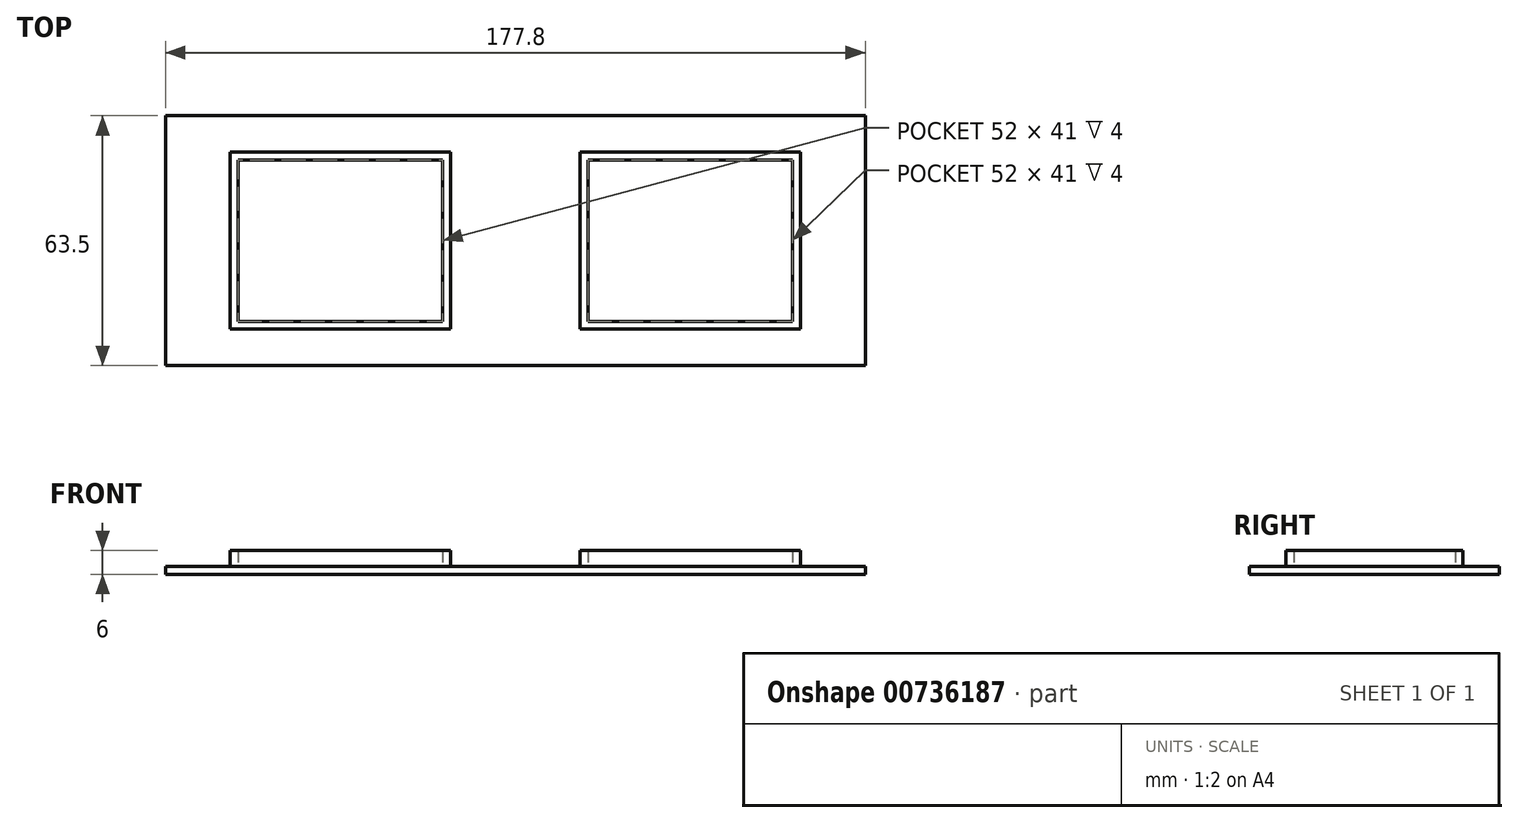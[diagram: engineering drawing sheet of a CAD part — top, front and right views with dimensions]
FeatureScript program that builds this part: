
annotation { "Feature Type Name" : "Feature", "Feature Type Description" : "" }
export const myFeature = defineFeature(function(context is Context, id is Id, definition is map)
    precondition{}
    {
        {
            var Q0;
            Q0=qCreatedBy(makeId("Top.planeOp"),FACE);
            var sketch = newSketch(context, id + "F0", { "sketchPlane" : qUnion([Q0])});
            skLineSegment(sketch, "E0.bottom", {"start": v(0, 0) * mm, "end": v(88.9, 0) * mm});
            skLineSegment(sketch, "E0.top", {"start": v(0, 63.5) * mm, "end": v(88.9, 63.5) * mm});
            skLineSegment(sketch, "E0.left", {"start": v(0, 0) * mm, "end": v(0, 63.5) * mm});
            skLineSegment(sketch, "E0.right", {"start": v(88.9, 0) * mm, "end": v(88.9, 63.5) * mm});
            skLineSegment(sketch, "E1", {"start": v(44.45, 0) * mm, "end": v(44.45, 63.5) * mm, "construction": true});
            skLineSegment(sketch, "E2", {"start": v(0, 31.75) * mm, "end": v(88.9, 31.75) * mm, "construction": true});
            skLineSegment(sketch, "E3.bottom", {"start": v(70.45, 52.25) * mm, "end": v(18.45, 52.25) * mm});
            skLineSegment(sketch, "E3.top", {"start": v(70.45, 11.25) * mm, "end": v(18.45, 11.25) * mm});
            skLineSegment(sketch, "E3.left", {"start": v(70.45, 52.25) * mm, "end": v(70.45, 11.25) * mm});
            skLineSegment(sketch, "E3.right", {"start": v(18.45, 52.25) * mm, "end": v(18.45, 11.25) * mm});
            skPoint(sketch, "E3.middle", {"position": v(44.45, 31.75) * mm});
            skLineSegment(sketch, "E4.bottom", {"start": v(16.45, 54.25) * mm, "end": v(72.45, 54.25) * mm});
            skLineSegment(sketch, "E4.top", {"start": v(16.45, 9.25) * mm, "end": v(72.45, 9.25) * mm});
            skLineSegment(sketch, "E4.left", {"start": v(16.45, 54.25) * mm, "end": v(16.45, 9.25) * mm});
            skLineSegment(sketch, "E4.right", {"start": v(72.45, 54.25) * mm, "end": v(72.45, 9.25) * mm});
            skSolve(sketch);
        }
        {
            var Q0;
            Q0=makeQuery(id+"F0.imprint","IMPRINT",FACE,{"disambiguationData":[TD([[makeQuery(id+"F0.imprint","IMPRINT",EDGE,{"derivedFrom":sQuery(id+"F0.wireOp",EDGE,"E3.bottom")}),-1.0]])]});
            extrude(context, id + "F1", {"entities" : qUnion([Q0]), "depth" : 6 * mm, "offsetDistance" : 25 * mm});
        }
        {
            var Q0;
            Q0=makeQuery(id+"F0.imprint","IMPRINT",FACE,{"disambiguationData":[TD([[makeQuery(id+"F0.imprint","IMPRINT",EDGE,{"derivedFrom":sQuery(id+"F0.wireOp",EDGE,"E0.bottom")}),1.0]])]});
            extrude(context, id + "F2", {"entities" : qUnion([Q0]), "operationType" : NewBodyOperationType.ADD, "depth" : 2 * mm, "offsetDistance" : 25 * mm});
        }
        {
            var Q0;
            Q0=makeQuery(id+"F0.imprint","IMPRINT",FACE,{"disambiguationData":[TD([[makeQuery(id+"F0.imprint","IMPRINT",EDGE,{"derivedFrom":sQuery(id+"F0.wireOp",EDGE,"E3.bottom")}),1.0]])]});
            extrude(context, id + "F3", {"entities" : qUnion([Q0]), "depth" : 2 * mm, "offsetDistance" : 25 * mm});
        }
        {
            var Q0;
            Q0=makeQuery(id+"F3.opExtrude","SWEPT_BODY",BODY,{"disambiguationData":[OSD([sQuery(id+"F0.wireOp",EDGE,"E3.bottom"),sQuery(id+"F0.wireOp",EDGE,"E3.top"),sQuery(id+"F0.wireOp",EDGE,"E3.left"),sQuery(id+"F0.wireOp",EDGE,"E3.right")])]});
            var Q1;
            Q1=makeQuery(id+"F1.opExtrude","SWEPT_BODY",BODY,{"disambiguationData":[OSD([sQuery(id+"F0.wireOp",EDGE,"E3.bottom"),sQuery(id+"F0.wireOp",EDGE,"E3.top"),sQuery(id+"F0.wireOp",EDGE,"E3.left"),sQuery(id+"F0.wireOp",EDGE,"E3.right"),sQuery(id+"F0.wireOp",EDGE,"E4.bottom"),sQuery(id+"F0.wireOp",EDGE,"E4.top"),sQuery(id+"F0.wireOp",EDGE,"E4.left"),sQuery(id+"F0.wireOp",EDGE,"E4.right")])]});
            var Q2;
            Q2=qCreatedBy(makeId("Right.planeOp"),FACE);
            mirror(context, id + "F4", {"operationType" : NewBodyOperationType.ADD, "entities" : qUnion([Q0, Q1]), "mirrorPlane" : qUnion([Q2])});
        }
    });
